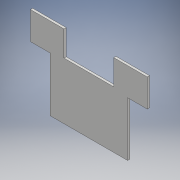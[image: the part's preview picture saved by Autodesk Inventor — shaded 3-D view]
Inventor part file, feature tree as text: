
AUTODESK INVENTOR PART (.ipt)
format: ipt  version: 2018 (Build 220112000, 112)  size: 109,056 bytes
history: native  units: mm
features: other x1, extrude x1, sketch x1
ambient origin geometry x8: Origin, YZ Plane, XZ Plane, XY Plane, X Axis, Y Axis, Z Axis, Center Point
bodies: Body1 (feature_tree)
feature tree (3):
  other  "ソリッド1"
  extrude  "押し出し1"  Depth=545.6mm
  sketch  "スケッチ1"
